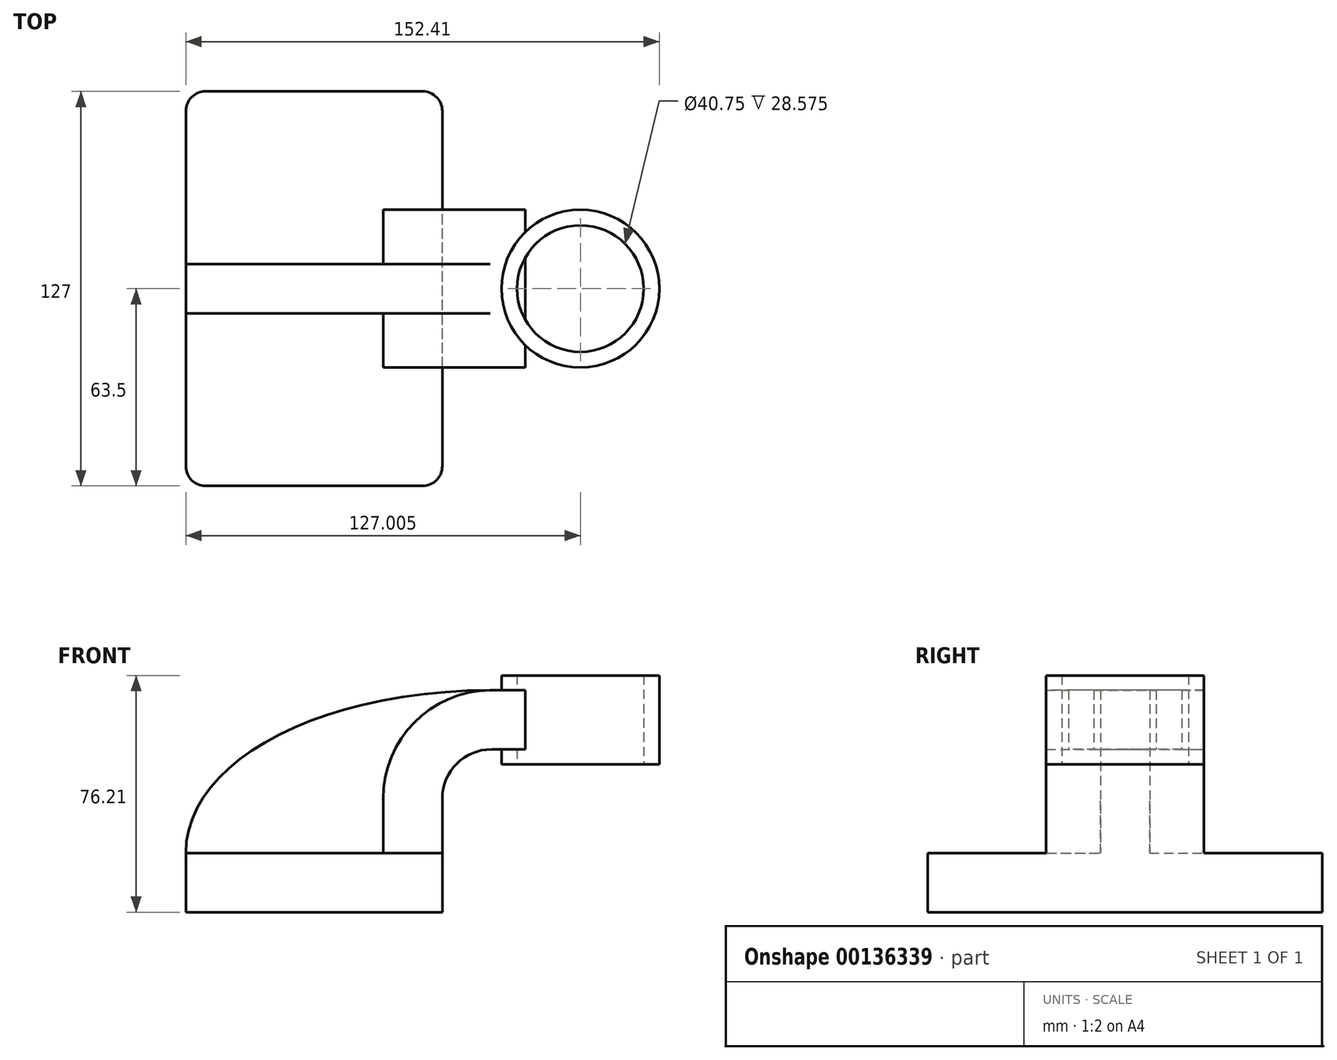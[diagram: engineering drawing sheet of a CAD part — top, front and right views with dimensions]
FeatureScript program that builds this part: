
annotation { "Feature Type Name" : "Feature", "Feature Type Description" : "" }
export const myFeature = defineFeature(function(context is Context, id is Id, definition is map)
    precondition{}
    {
        {
            var Q0;
            Q0=qCreatedBy(makeId("Front.planeOp"),FACE);
            var sketch = newSketch(context, id + "F0", { "sketchPlane" : qUnion([Q0])});
            skLineSegment(sketch, "E0.bottom", {"start": v(41.28, -9.52) * mm, "end": v(-41.27, -9.52) * mm});
            skLineSegment(sketch, "E0.top", {"start": v(41.27, 9.53) * mm, "end": v(-41.28, 9.53) * mm});
            skLineSegment(sketch, "E0.left", {"start": v(41.28, -9.52) * mm, "end": v(41.28, 9.53) * mm});
            skLineSegment(sketch, "E0.right", {"start": v(-41.28, -9.52) * mm, "end": v(-41.28, 9.53) * mm});
            skPoint(sketch, "E0.middle", {"position": v(0, 0) * mm});
            skLineSegment(sketch, "E1.bottom", {"start": v(111.12, 38.1) * mm, "end": v(60.33, 38.1) * mm});
            skLineSegment(sketch, "E1.top", {"start": v(111.12, 66.68) * mm, "end": v(60.33, 66.68) * mm});
            skLineSegment(sketch, "E1.left", {"start": v(111.12, 38.1) * mm, "end": v(111.12, 66.68) * mm});
            skLineSegment(sketch, "E1.right", {"start": v(60.33, 38.1) * mm, "end": v(60.33, 66.68) * mm});
            skLineSegment(sketch, "E2", {"start": v(41.27, 9.53) * mm, "end": v(41.27, 27) * mm});
            skArc(sketch, "E3", {"start": v(41.27, 27) * mm, "mid": v(45.92, 38.23) * mm, "end": v(57.15, 42.88) * mm});
            skLineSegment(sketch, "E4", {"start": v(57.15, 42.88) * mm, "end": v(85.72, 42.88) * mm});
            skPoint(sketch, "E4.endSnap0", {"position": v(85.72, 38.1) * mm});
            skLineSegment(sketch, "E5.0", {"start": v(57.15, 61.93) * mm, "end": v(85.72, 61.93) * mm});
            skArc(sketch, "E5.1", {"start": v(22.23, 27) * mm, "mid": v(32.45, 51.7) * mm, "end": v(57.15, 61.93) * mm});
            skLineSegment(sketch, "E5.2", {"start": v(22.22, 9.53) * mm, "end": v(22.22, 27) * mm});
            skLineSegment(sketch, "E6", {"start": v(85.72, 38.1) * mm, "end": v(85.72, 66.68) * mm});
            skFitSpline(sketch, "E7", {"points": [v(57.15, 61.93) * mm, v(-41.28, 9.52) * mm], "startDerivative": vector(-171.45, -0.87) * mm, "endDerivative": vector(0, -86.32) * mm});
            skLineSegment(sketch, "E8.bottom", {"start": v(68, 38.1) * mm, "end": v(106.1, 38.1) * mm});
            skLineSegment(sketch, "E8.top", {"start": v(68, 66.68) * mm, "end": v(106.1, 66.68) * mm});
            skLineSegment(sketch, "E8.left", {"start": v(68, 38.1) * mm, "end": v(68, 66.68) * mm});
            skLineSegment(sketch, "E8.right", {"start": v(106.1, 38.1) * mm, "end": v(106.1, 66.68) * mm});
            skSolve(sketch);
        }
        {
            var Q0;
            Q0=makeQuery(id+"F0.imprint","IMPRINT",FACE,{"disambiguationData":[TD([[makeQuery(id+"F0.imprint","IMPRINT",EDGE,{"derivedFrom":sQuery(id+"F0.wireOp",EDGE,"E0.bottom")}),-1.0]])]});
            extrude(context, id + "F1", {"entities" : qUnion([Q0]), "endBound" : BoundingType.SYMMETRIC, "depth" : 127 * mm});
        }
        {
            var Q0;
            {var subQ6=sQuery(id+"F0.wireOp",EDGE,"E2");Q0=makeQuery(id+"F0.imprint","IMPRINT",FACE,{"disambiguationData":[TD([[makeQuery(id+"F0.imprint","IMPRINT",EDGE,{"derivedFrom":subQ6}),1.0]])]});}
            var Q1;
            {var subQ0=sQuery(id+"F0.wireOp",EDGE,"E4");var subQ1=sQuery(id+"F0.wireOp",EDGE,"E1.right");var subQ2=makeQuery(id+"F0.imprint","INTERSECT",VERTEX,{"derivedFrom":[subQ1,subQ0]});Q1=makeQuery(id+"F0.imprint","IMPRINT",FACE,{"disambiguationData":[TD([[makeQuery(id+"F0.imprint","IMPRINT",EDGE,{"disambiguationData":[TD([[subQ2,-1.0]])],"derivedFrom":subQ1}),-1.0]])]});}
            extrude(context, id + "F2", {"entities" : qUnion([Q0, Q1]), "operationType" : NewBodyOperationType.ADD, "endBound" : BoundingType.SYMMETRIC, "depth" : 50.8 * mm});
        }
        {
            var Q0;
            {var subQ3=sQuery(id+"F0.wireOp",EDGE,"E5.2");Q0=makeQuery(id+"F0.imprint","IMPRINT",FACE,{"disambiguationData":[TD([[makeQuery(id+"F0.imprint","IMPRINT",EDGE,{"derivedFrom":subQ3}),1.0]])]});}
            extrude(context, id + "F3", {"entities" : qUnion([Q0]), "operationType" : NewBodyOperationType.ADD, "endBound" : BoundingType.SYMMETRIC, "depth" : 15.88 * mm});
        }
        {
            var Q0;
            {var subQ0=sQuery(id+"F0.wireOp",EDGE,"E1.left");Q0=makeQuery(id+"F0.imprint","IMPRINT",FACE,{"disambiguationData":[TD([[makeQuery(id+"F0.imprint","IMPRINT",EDGE,{"derivedFrom":subQ0}),1.0]])]});}
            var Q1;
            Q1=sQuery(id+"F0.wireOp",EDGE,"E6");
            revolve(context, id + "F4", {"operationType" : NewBodyOperationType.ADD, "entities" : qUnion([Q0]), "axis" : qUnion([Q1]), "revolveType" : RevolveType.FULL});
        }
        {
            var Q0;
            Q0=makeQuery(id+"F1.opExtrude","CAP_EDGE",EDGE,{"disambiguationData":[OSD([sQuery(id+"F0.wireOp",EDGE,"E0.left")])],"isStart":false});
            var Q1;
            Q1=makeQuery(id+"F1.opExtrude","CAP_EDGE",EDGE,{"disambiguationData":[OSD([sQuery(id+"F0.wireOp",EDGE,"E0.right")])],"isStart":false});
            var Q2;
            Q2=makeQuery(id+"F1.opExtrude","CAP_EDGE",EDGE,{"disambiguationData":[OSD([sQuery(id+"F0.wireOp",EDGE,"E0.left")])],"isStart":true});
            var Q3;
            Q3=makeQuery(id+"F1.opExtrude","CAP_EDGE",EDGE,{"disambiguationData":[OSD([sQuery(id+"F0.wireOp",EDGE,"E0.right")])],"isStart":true});
            fillet(context, id + "F5", {"entities" : qUnion([Q0, Q1, Q2, Q3]), "radius" : 6.35 * mm, "tangentPropagation" : true, "allowEdgeOverflow" : false});
        }
    });
